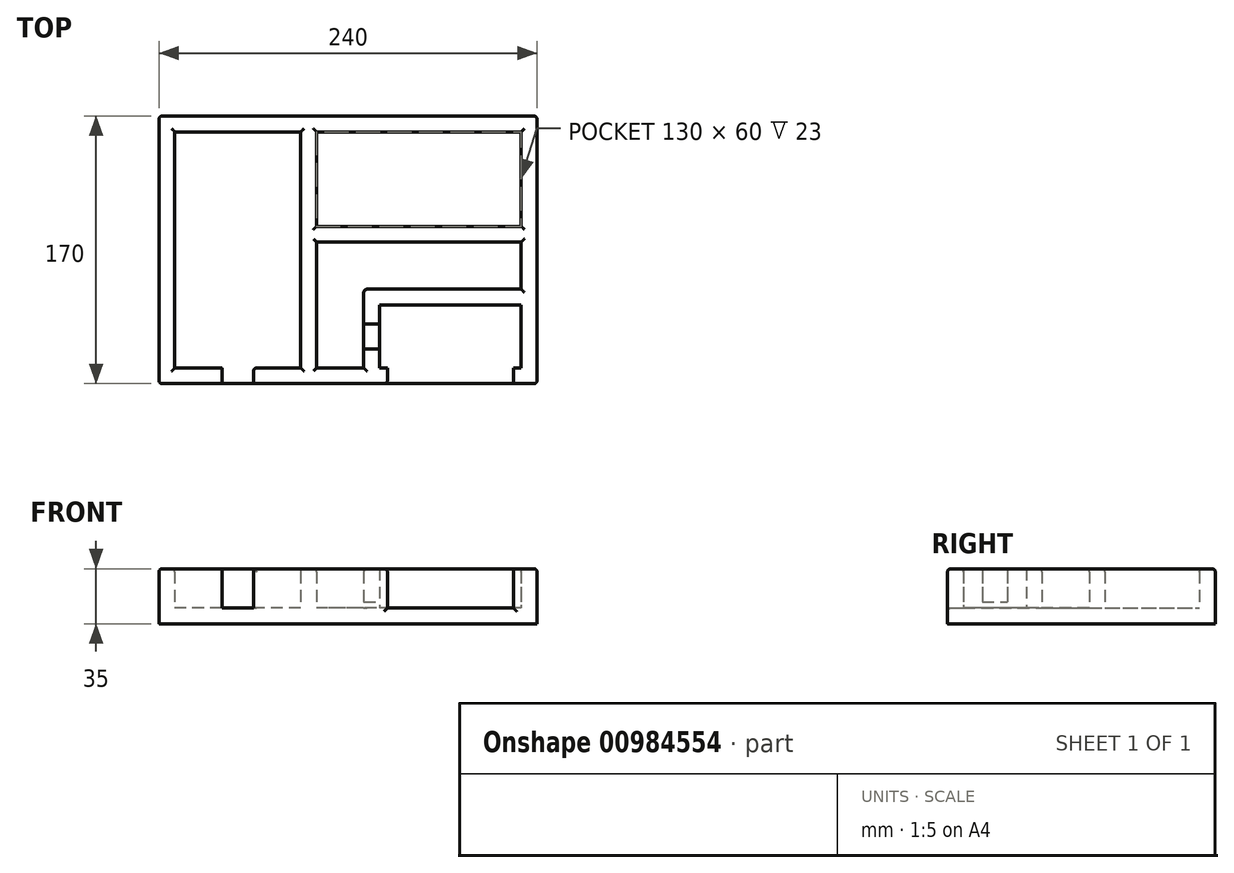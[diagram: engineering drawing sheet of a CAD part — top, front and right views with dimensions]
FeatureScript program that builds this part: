
annotation { "Feature Type Name" : "Feature", "Feature Type Description" : "" }
export const myFeature = defineFeature(function(context is Context, id is Id, definition is map)
    precondition{}
    {
        {
            var Q0;
            Q0=qCreatedBy(makeId("Top.planeOp"),FACE);
            var sketch = newSketch(context, id + "F0", { "sketchPlane" : qUnion([Q0])});
            skLineSegment(sketch, "E0.bottom", {"start": v(120, -85) * mm, "end": v(-120, -85) * mm});
            skLineSegment(sketch, "E0.top", {"start": v(120, 85) * mm, "end": v(-120, 85) * mm});
            skLineSegment(sketch, "E0.left", {"start": v(120, -85) * mm, "end": v(120, 85) * mm});
            skLineSegment(sketch, "E0.right", {"start": v(-120, -85) * mm, "end": v(-120, 85) * mm});
            skPoint(sketch, "E0.middle", {"position": v(0, 0) * mm});
            skLineSegment(sketch, "E1.bottom", {"start": v(-30, -75) * mm, "end": v(-110, -75) * mm});
            skLineSegment(sketch, "E1.top", {"start": v(-30, 75) * mm, "end": v(-110, 75) * mm});
            skLineSegment(sketch, "E1.left", {"start": v(-30, -75) * mm, "end": v(-30, 75) * mm});
            skLineSegment(sketch, "E1.right", {"start": v(-110, -75) * mm, "end": v(-110, 75) * mm});
            skPoint(sketch, "E1.middle", {"position": v(-70, 0) * mm});
            skLineSegment(sketch, "E2", {"start": v(-120, 0) * mm, "end": v(-110, 0) * mm, "construction": true});
            skLineSegment(sketch, "E3.bottom", {"start": v(110, 15) * mm, "end": v(-20, 15) * mm});
            skLineSegment(sketch, "E3.top", {"start": v(110, 75) * mm, "end": v(-20, 75) * mm});
            skLineSegment(sketch, "E3.left", {"start": v(110, 15) * mm, "end": v(110, 75) * mm});
            skLineSegment(sketch, "E3.right", {"start": v(-20, 15) * mm, "end": v(-20, 75) * mm});
            skPoint(sketch, "E3.middle", {"position": v(45, 45) * mm});
            skLineSegment(sketch, "E4.bottom", {"start": v(110, -35) * mm, "end": v(20, -35) * mm});
            skLineSegment(sketch, "E4.top", {"start": v(110, -75) * mm, "end": v(20, -75) * mm});
            skLineSegment(sketch, "E4.left", {"start": v(110, -35) * mm, "end": v(110, -75) * mm});
            skLineSegment(sketch, "E4.right", {"start": v(20, -35) * mm, "end": v(20, -75) * mm});
            skPoint(sketch, "E4.middle", {"position": v(65, -55) * mm});
            skLineSegment(sketch, "E5.bottom", {"start": v(110, -25) * mm, "end": v(-20, -25) * mm});
            skLineSegment(sketch, "E5.top", {"start": v(110, 5) * mm, "end": v(-20, 5) * mm});
            skLineSegment(sketch, "E5.left", {"start": v(110, -25) * mm, "end": v(110, 5) * mm});
            skLineSegment(sketch, "E5.right", {"start": v(-20, -25) * mm, "end": v(-20, 5) * mm});
            skPoint(sketch, "E5.middle", {"position": v(45, -10) * mm});
            skLineSegment(sketch, "E6.bottom", {"start": v(10, -25) * mm, "end": v(-20, -25) * mm});
            skLineSegment(sketch, "E6.top", {"start": v(10, -75) * mm, "end": v(-20, -75) * mm});
            skLineSegment(sketch, "E6.left", {"start": v(10, -25) * mm, "end": v(10, -75) * mm});
            skLineSegment(sketch, "E6.right", {"start": v(-20, -25) * mm, "end": v(-20, -75) * mm});
            skPoint(sketch, "E6.middle", {"position": v(-5, -50) * mm});
            skLineSegment(sketch, "E7.bottom", {"start": v(105, -85) * mm, "end": v(25, -85) * mm});
            skLineSegment(sketch, "E7.top", {"start": v(105, -75) * mm, "end": v(25, -75) * mm});
            skLineSegment(sketch, "E7.left", {"start": v(105, -85) * mm, "end": v(105, -75) * mm});
            skLineSegment(sketch, "E7.right", {"start": v(25, -85) * mm, "end": v(25, -75) * mm});
            skPoint(sketch, "E7.middle", {"position": v(65, -80) * mm});
            skPoint(sketch, "E8", {"position": v(65, -75) * mm});
            skSolve(sketch);
        }
        {
            var Q0;
            Q0=makeQuery(id+"F0.imprint","IMPRINT",FACE,{"disambiguationData":[TD([[makeQuery(id+"F0.imprint","IMPRINT",EDGE,{"derivedFrom":sQuery(id+"F0.wireOp",EDGE,"E0.top")}),1.0]])]});
            extrude(context, id + "F1", {"entities" : qUnion([Q0]), "depth" : 25 * mm, "offsetDistance" : 25 * mm});
        }
        {
            var Q0;
            Q0=makeQuery(id+"F1.opExtrude","CAP_FACE",FACE,{"disambiguationData":[OSD([sQuery(id+"F0.wireOp",EDGE,"E0.bottom"),sQuery(id+"F0.wireOp",EDGE,"E0.top"),sQuery(id+"F0.wireOp",EDGE,"E0.left"),sQuery(id+"F0.wireOp",EDGE,"E0.right"),sQuery(id+"F0.wireOp",EDGE,"E1.bottom"),sQuery(id+"F0.wireOp",EDGE,"E1.top"),sQuery(id+"F0.wireOp",EDGE,"E1.left"),sQuery(id+"F0.wireOp",EDGE,"E1.right"),sQuery(id+"F0.wireOp",EDGE,"E3.bottom"),sQuery(id+"F0.wireOp",EDGE,"E3.top"),sQuery(id+"F0.wireOp",EDGE,"E3.left"),sQuery(id+"F0.wireOp",EDGE,"E3.right"),sQuery(id+"F0.wireOp",EDGE,"E4.bottom"),sQuery(id+"F0.wireOp",EDGE,"E4.top"),sQuery(id+"F0.wireOp",EDGE,"E4.left"),sQuery(id+"F0.wireOp",EDGE,"E4.right"),sQuery(id+"F0.wireOp",EDGE,"E5.bottom"),sQuery(id+"F0.wireOp",EDGE,"E5.top"),sQuery(id+"F0.wireOp",EDGE,"E5.left"),sQuery(id+"F0.wireOp",EDGE,"E5.right"),sQuery(id+"F0.wireOp",EDGE,"E6.top"),sQuery(id+"F0.wireOp",EDGE,"E6.left"),sQuery(id+"F0.wireOp",EDGE,"E6.right"),sQuery(id+"F0.wireOp",EDGE,"E7.left"),sQuery(id+"F0.wireOp",EDGE,"E7.right")])],"isStart":true});
            var sketch = newSketch(context, id + "F2", { "sketchPlane" : qUnion([Q0])});
            skLineSegment(sketch, "E9.bottom", {"start": v(-120, 85) * mm, "end": v(120, 85) * mm});
            skLineSegment(sketch, "E9.top", {"start": v(-120, -85) * mm, "end": v(120, -85) * mm});
            skLineSegment(sketch, "E9.left", {"start": v(-120, 85) * mm, "end": v(-120, -85) * mm});
            skLineSegment(sketch, "E9.right", {"start": v(120, 85) * mm, "end": v(120, -85) * mm});
            skLineSegment(sketch, "E10", {"start": v(-110, 75) * mm, "end": v(-110, 85) * mm, "construction": true});
            skLineSegment(sketch, "E11", {"start": v(-30, 75) * mm, "end": v(-30, 85) * mm, "construction": true});
            skSolve(sketch);
        }
        {
            var Q0;
            Q0 = qSketchRegion(id + "F2", true);
            extrude(context, id + "F3", {"entities" : qUnion([Q0]), "operationType" : NewBodyOperationType.ADD, "depth" : 10 * mm, "offsetDistance" : 25 * mm});
        }
        {
            var Q0;
            Q0=makeQuery(id+"F1.opExtrude","SWEPT_FACE",FACE,{"disambiguationData":[OSD([sQuery(id+"F0.wireOp",EDGE,"E1.bottom")])]});
            var sketch = newSketch(context, id + "F4", { "sketchPlane" : qUnion([Q0])});
            skLineSegment(sketch, "E12.bottom", {"start": v(60, 25) * mm, "end": v(80, 25) * mm});
            skLineSegment(sketch, "E12.top", {"start": v(60, 0) * mm, "end": v(80, 0) * mm});
            skLineSegment(sketch, "E12.left", {"start": v(60, 25) * mm, "end": v(60, 0) * mm});
            skLineSegment(sketch, "E12.right", {"start": v(80, 25) * mm, "end": v(80, 0) * mm});
            skLineSegment(sketch, "E13", {"start": v(30, 12.5) * mm, "end": v(60, 12.5) * mm, "construction": true});
            skLineSegment(sketch, "E14", {"start": v(80, 12.5) * mm, "end": v(110, 12.5) * mm, "construction": true});
            skSolve(sketch);
        }
        {
            var Q0;
            Q0=makeQuery(id+"F4.imprint","IMPRINT",FACE,{"disambiguationData":[TD([[makeQuery(id+"F4.imprint","IMPRINT",EDGE,{"derivedFrom":sQuery(id+"F4.wireOp",EDGE,"E12.bottom")}),-1.0]])]});
            extrude(context, id + "F5", {"entities" : qUnion([Q0]), "operationType" : NewBodyOperationType.REMOVE, "oppositeDirection" : true, "depth" : 10 * mm, "offsetDistance" : 25 * mm});
        }
        {
            var Q0;
            Q0=makeQuery(id+"F1.opExtrude","CAP_EDGE",EDGE,{"disambiguationData":[OSD([sQuery(id+"F0.wireOp",EDGE,"E1.right")])],"isStart":false});
            var Q1;
            Q1=makeQuery(id+"F1.opExtrude","CAP_EDGE",EDGE,{"disambiguationData":[OSD([sQuery(id+"F0.wireOp",EDGE,"E0.right")])],"isStart":false});
            var Q2;
            {var subQ0=sQuery(id+"F0.wireOp",EDGE,"E0.right");var subQ1=sQuery(id+"F0.wireOp",EDGE,"E0.bottom");var subQ4=makeQuery(id+"F0.imprint","IMPRINT",EDGE,{"disambiguationData":[TD([[makeQuery(id+"F0.imprint","INTERSECT",VERTEX,{"derivedFrom":[subQ1,subQ0]}),1.0]])],"derivedFrom":subQ1});Q2=makeQuery(id+"F5.boolean.opBoolean","SPLIT",EDGE,{"disambiguationData":[TD([makeQuery(id+"F1.opExtrude","SWEPT_FACE",FACE,{"disambiguationData":[OSD([subQ0])]})])],"derivedFrom":makeQuery(id+"F1.opExtrude","CAP_EDGE",EDGE,{"disambiguationData":[OSD([subQ1]),TDD([subQ4])],"isStart":false})});}
            var Q3;
            {var subQ0=sQuery(id+"F0.wireOp",EDGE,"E1.right");var subQ1=sQuery(id+"F0.wireOp",EDGE,"E1.bottom");Q3=makeQuery(id+"F5.boolean.opBoolean","SPLIT",EDGE,{"disambiguationData":[TD([makeQuery(id+"F1.opExtrude","SWEPT_FACE",FACE,{"disambiguationData":[OSD([subQ0])]})])],"derivedFrom":makeQuery(id+"F1.opExtrude","CAP_EDGE",EDGE,{"disambiguationData":[OSD([subQ1])],"isStart":false})});}
            var Q4;
            Q4=makeQuery(id+"F5.boolean.opBoolean","COPY",EDGE,{"derivedFrom":makeQuery(id+"F5.opExtrude","CAP_EDGE",EDGE,{"disambiguationData":[OSD([sQuery(id+"F4.wireOp",EDGE,"E12.left")])],"isStart":false})});
            var Q5;
            Q5=makeQuery(id+"F5.boolean.opBoolean","COPY",EDGE,{"derivedFrom":makeQuery(id+"F5.opExtrude","CAP_EDGE",EDGE,{"disambiguationData":[OSD([sQuery(id+"F4.wireOp",EDGE,"E12.right")])],"isStart":false})});
            var Q6;
            Q6=makeQuery(id+"F5.boolean.opBoolean","COPY",EDGE,{"derivedFrom":makeQuery(id+"F5.opExtrude","CAP_EDGE",EDGE,{"disambiguationData":[OSD([sQuery(id+"F4.wireOp",EDGE,"E12.right")])],"isStart":true})});
            var Q7;
            Q7=makeQuery(id+"F5.boolean.opBoolean","COPY",EDGE,{"derivedFrom":makeQuery(id+"F5.opExtrude","SWEPT_EDGE",EDGE,{"disambiguationData":[OSD([sQuery(id+"F0.wireOp",EDGE,"E1.bottom"),sQuery(id+"F4.wireOp",EDGE,"E12.bottom"),sQuery(id+"F4.wireOp",EDGE,"E12.left")])]})});
            var Q8;
            Q8=makeQuery(id+"F5.boolean.opBoolean","COPY",EDGE,{"derivedFrom":makeQuery(id+"F5.opExtrude","CAP_EDGE",EDGE,{"disambiguationData":[OSD([sQuery(id+"F4.wireOp",EDGE,"E12.left")])],"isStart":true})});
            var Q9;
            Q9=makeQuery(id+"F1.opExtrude","CAP_EDGE",EDGE,{"disambiguationData":[OSD([sQuery(id+"F0.wireOp",EDGE,"E1.left")])],"isStart":false});
            var Q10;
            {var subQ0=sQuery(id+"F0.wireOp",EDGE,"E1.left");var subQ1=sQuery(id+"F0.wireOp",EDGE,"E1.bottom");Q10=makeQuery(id+"F5.boolean.opBoolean","SPLIT",EDGE,{"disambiguationData":[TD([makeQuery(id+"F1.opExtrude","SWEPT_FACE",FACE,{"disambiguationData":[OSD([subQ0])]})])],"derivedFrom":makeQuery(id+"F1.opExtrude","CAP_EDGE",EDGE,{"disambiguationData":[OSD([subQ1])],"isStart":false})});}
            var Q11;
            Q11=makeQuery(id+"F5.boolean.opBoolean","COPY",EDGE,{"derivedFrom":makeQuery(id+"F5.opExtrude","CAP_EDGE",EDGE,{"disambiguationData":[OSD([sQuery(id+"F4.wireOp",EDGE,"E12.top")])],"isStart":false})});
            var Q12;
            Q12=makeQuery(id+"F1.opExtrude","CAP_EDGE",EDGE,{"disambiguationData":[OSD([sQuery(id+"F0.wireOp",EDGE,"E5.right"),sQuery(id+"F0.wireOp",EDGE,"E6.right")])],"isStart":false});
            var Q13;
            Q13=makeQuery(id+"F1.opExtrude","CAP_EDGE",EDGE,{"disambiguationData":[OSD([sQuery(id+"F0.wireOp",EDGE,"E5.bottom")])],"isStart":false});
            var Q14;
            Q14=makeQuery(id+"F1.opExtrude","CAP_EDGE",EDGE,{"disambiguationData":[OSD([sQuery(id+"F0.wireOp",EDGE,"E6.top")])],"isStart":false});
            var Q15;
            Q15=makeQuery(id+"F1.opExtrude","SWEPT_EDGE",EDGE,{"disambiguationData":[OSD([sQuery(id+"F0.wireOp",EDGE,"E5.bottom"),sQuery(id+"F0.wireOp",EDGE,"E6.bottom"),sQuery(id+"F0.wireOp",EDGE,"E6.left")])]});
            var Q16;
            Q16=makeQuery(id+"F1.opExtrude","CAP_EDGE",EDGE,{"disambiguationData":[OSD([sQuery(id+"F0.wireOp",EDGE,"E6.left")])],"isStart":false});
            var Q17;
            Q17=makeQuery(id+"F1.opExtrude","SWEPT_EDGE",EDGE,{"disambiguationData":[OSD([sQuery(id+"F0.wireOp",EDGE,"E0.bottom"),sQuery(id+"F0.wireOp",EDGE,"E7.bottom"),sQuery(id+"F0.wireOp",EDGE,"E7.right")])]});
            var Q18;
            {var subQ0=sQuery(id+"F0.wireOp",EDGE,"E0.right");var subQ1=sQuery(id+"F0.wireOp",EDGE,"E0.bottom");var subQ2=sQuery(id+"F0.wireOp",EDGE,"E7.right");var subQ4=makeQuery(id+"F0.imprint","IMPRINT",EDGE,{"disambiguationData":[TD([[makeQuery(id+"F0.imprint","INTERSECT",VERTEX,{"derivedFrom":[subQ1,subQ0]}),1.0]])],"derivedFrom":subQ1});Q18=makeQuery(id+"F5.boolean.opBoolean","SPLIT",EDGE,{"disambiguationData":[TD([makeQuery(id+"F1.opExtrude","SWEPT_FACE",FACE,{"disambiguationData":[OSD([subQ2])]})])],"derivedFrom":makeQuery(id+"F1.opExtrude","CAP_EDGE",EDGE,{"disambiguationData":[OSD([subQ1]),TDD([subQ4])],"isStart":false})});}
            var Q19;
            Q19=makeQuery(id+"F3.opExtrude","CAP_EDGE",EDGE,{"disambiguationData":[OSD([sQuery(id+"F2.wireOp",EDGE,"E9.bottom")])],"isStart":true});
            var Q20;
            Q20=makeQuery(id+"F1.opExtrude","SWEPT_EDGE",EDGE,{"disambiguationData":[OSD([sQuery(id+"F0.wireOp",EDGE,"E0.bottom"),sQuery(id+"F0.wireOp",EDGE,"E7.bottom"),sQuery(id+"F0.wireOp",EDGE,"E7.left")])]});
            var Q21;
            {var subQ0=sQuery(id+"F0.wireOp",EDGE,"E0.bottom");Q21=makeQuery(id+"F1.opExtrude","CAP_EDGE",EDGE,{"disambiguationData":[OSD([subQ0]),TDD([makeQuery(id+"F0.imprint","IMPRINT",EDGE,{"disambiguationData":[TD([[makeQuery(id+"F0.imprint","INTERSECT",VERTEX,{"derivedFrom":[subQ0,sQuery(id+"F0.wireOp",EDGE,"E0.left")]}),-1.0]])],"derivedFrom":subQ0})])],"isStart":false});}
            var Q22;
            Q22=makeQuery(id+"F1.opExtrude","CAP_EDGE",EDGE,{"disambiguationData":[OSD([sQuery(id+"F0.wireOp",EDGE,"E0.left")])],"isStart":false});
            var Q23;
            Q23=makeQuery(id+"F3.boolean.opBoolean","MERGE",EDGE,{"derivedFrom":[makeQuery(id+"F1.opExtrude","SWEPT_EDGE",EDGE,{"disambiguationData":[OSD([sQuery(id+"F0.wireOp",EDGE,"E0.bottom"),sQuery(id+"F0.wireOp",EDGE,"E0.left")])]}),makeQuery(id+"F3.opExtrude","SWEPT_EDGE",EDGE,{"disambiguationData":[OSD([sQuery(id+"F2.wireOp",EDGE,"E9.bottom"),sQuery(id+"F2.wireOp",EDGE,"E9.right")])]})]});
            var Q24;
            Q24=makeQuery(id+"F3.boolean.opBoolean","MERGE",EDGE,{"derivedFrom":[makeQuery(id+"F1.opExtrude","SWEPT_EDGE",EDGE,{"disambiguationData":[OSD([sQuery(id+"F0.wireOp",EDGE,"E0.bottom"),sQuery(id+"F0.wireOp",EDGE,"E0.right")])]}),makeQuery(id+"F3.opExtrude","SWEPT_EDGE",EDGE,{"disambiguationData":[OSD([sQuery(id+"F2.wireOp",EDGE,"E9.bottom"),sQuery(id+"F2.wireOp",EDGE,"E9.left")])]})]});
            var Q25;
            Q25=makeQuery(id+"F1.opExtrude","CAP_EDGE",EDGE,{"disambiguationData":[OSD([sQuery(id+"F0.wireOp",EDGE,"E5.top")])],"isStart":false});
            var Q26;
            Q26=makeQuery(id+"F1.opExtrude","CAP_EDGE",EDGE,{"disambiguationData":[OSD([sQuery(id+"F0.wireOp",EDGE,"E3.bottom")])],"isStart":false});
            var Q27;
            Q27=makeQuery(id+"F1.opExtrude","CAP_EDGE",EDGE,{"disambiguationData":[OSD([sQuery(id+"F0.wireOp",EDGE,"E3.right")])],"isStart":false});
            var Q28;
            Q28=makeQuery(id+"F3.boolean.opBoolean","MERGE",EDGE,{"derivedFrom":[makeQuery(id+"F1.opExtrude","SWEPT_EDGE",EDGE,{"disambiguationData":[OSD([sQuery(id+"F0.wireOp",EDGE,"E0.top"),sQuery(id+"F0.wireOp",EDGE,"E0.right")])]}),makeQuery(id+"F3.opExtrude","SWEPT_EDGE",EDGE,{"disambiguationData":[OSD([sQuery(id+"F2.wireOp",EDGE,"E9.top"),sQuery(id+"F2.wireOp",EDGE,"E9.left")])]})]});
            var Q29;
            Q29=makeQuery(id+"F3.boolean.opBoolean","MERGE",EDGE,{"derivedFrom":[makeQuery(id+"F1.opExtrude","SWEPT_EDGE",EDGE,{"disambiguationData":[OSD([sQuery(id+"F0.wireOp",EDGE,"E0.top"),sQuery(id+"F0.wireOp",EDGE,"E0.left")])]}),makeQuery(id+"F3.opExtrude","SWEPT_EDGE",EDGE,{"disambiguationData":[OSD([sQuery(id+"F2.wireOp",EDGE,"E9.top"),sQuery(id+"F2.wireOp",EDGE,"E9.right")])]})]});
            var Q30;
            Q30=makeQuery(id+"F1.opExtrude","CAP_EDGE",EDGE,{"disambiguationData":[OSD([sQuery(id+"F0.wireOp",EDGE,"E0.top")])],"isStart":false});
            var Q31;
            Q31=makeQuery(id+"F1.opExtrude","CAP_EDGE",EDGE,{"disambiguationData":[OSD([sQuery(id+"F0.wireOp",EDGE,"E3.top")])],"isStart":false});
            var Q32;
            Q32=makeQuery(id+"F1.opExtrude","CAP_EDGE",EDGE,{"disambiguationData":[OSD([sQuery(id+"F0.wireOp",EDGE,"E3.left")])],"isStart":false});
            var Q33;
            Q33=makeQuery(id+"F1.opExtrude","CAP_EDGE",EDGE,{"disambiguationData":[OSD([sQuery(id+"F0.wireOp",EDGE,"E5.left")])],"isStart":false});
            var Q34;
            Q34=makeQuery(id+"F5.boolean.opBoolean","COPY",EDGE,{"derivedFrom":makeQuery(id+"F5.opExtrude","SWEPT_EDGE",EDGE,{"disambiguationData":[OSD([sQuery(id+"F0.wireOp",EDGE,"E1.bottom"),sQuery(id+"F4.wireOp",EDGE,"E12.bottom"),sQuery(id+"F4.wireOp",EDGE,"E12.right")])]})});
            var Q35;
            Q35=makeQuery(id+"F1.opExtrude","CAP_EDGE",EDGE,{"disambiguationData":[OSD([sQuery(id+"F0.wireOp",EDGE,"E7.right")])],"isStart":false});
            var Q36;
            Q36=makeQuery(id+"F1.opExtrude","CAP_EDGE",EDGE,{"disambiguationData":[OSD([sQuery(id+"F0.wireOp",EDGE,"E7.left")])],"isStart":false});
            var Q37;
            Q37=makeQuery(id+"F1.opExtrude","CAP_EDGE",EDGE,{"disambiguationData":[OSD([sQuery(id+"F0.wireOp",EDGE,"E1.top")])],"isStart":false});
            fillet(context, id + "F6", {"entities" : qUnion([Q0, Q1, Q2, Q3, Q4, Q5, Q6, Q7, Q8, Q9, Q10, Q11, Q12, Q13, Q14, Q15, Q16, Q17, Q18, Q19, Q20, Q21, Q22, Q23, Q24, Q25, Q26, Q27, Q28, Q29, Q30, Q31, Q32, Q33, Q34, Q35, Q36, Q37]), "radius" : 2 * mm, "tangentPropagation" : true, "allowEdgeOverflow" : false});
        }
        {
            var Q0;
            Q0=makeQuery(id+"F1.opExtrude","SWEPT_FACE",FACE,{"disambiguationData":[OSD([sQuery(id+"F0.wireOp",EDGE,"E4.right")])]});
            var sketch = newSketch(context, id + "F7", { "sketchPlane" : qUnion([Q0])});
            skLineSegment(sketch, "E15.bottom", {"start": v(-63, 25) * mm, "end": v(-47, 25) * mm});
            skLineSegment(sketch, "E15.top", {"start": v(-63, 4) * mm, "end": v(-47, 4) * mm});
            skLineSegment(sketch, "E15.left", {"start": v(-63, 25) * mm, "end": v(-63, 4) * mm});
            skLineSegment(sketch, "E15.right", {"start": v(-47, 25) * mm, "end": v(-47, 4) * mm});
            skSolve(sketch);
        }
        {
            var Q0;
            Q0=makeQuery(id+"F7.imprint","IMPRINT",FACE,{"disambiguationData":[TD([[makeQuery(id+"F7.imprint","IMPRINT",EDGE,{"derivedFrom":sQuery(id+"F7.wireOp",EDGE,"E15.bottom")}),1.0]])]});
            extrude(context, id + "F8", {"entities" : qUnion([Q0]), "operationType" : NewBodyOperationType.REMOVE, "oppositeDirection" : true, "depth" : 10 * mm, "offsetDistance" : 25 * mm});
        }
    });
